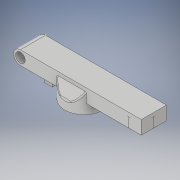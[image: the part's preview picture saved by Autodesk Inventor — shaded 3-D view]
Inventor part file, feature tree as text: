
AUTODESK INVENTOR PART (.ipt)
format: ipt  version: 2019 (Build 230136000, 136)  size: 247,808 bytes
history: native  units: in
note: dims shown in document units (in); Inventor stores cm internally (conversion verified against a paired STEP export)
features: sketch x9, extrude x5, chamfer x2, fillet x2
ambient origin geometry x8: Origin, YZ Plane, XZ Plane, XY Plane, X Axis, Y Axis, Z Axis, Center Point
bodies: Solid1 (feature_tree)
feature tree (18):
  extrude  "Extrusion1"  Depth=2.4606in
  extrude  "Extrusion2"  Depth=0.5118in TaperAngle=0.0deg
  extrude  "Extrusion3"  Depth=0.1969in TaperAngle=0.0deg
  sketch  "Sketch4"  dims[d9=2.2047in]
  chamfer  "Chamfer1"  Distance=0.1969in
  chamfer  "Chamfer2"  Distance=0.1181in Angle=120.0deg
  extrude  "Extrusion4"  Depth=0.2362in TaperAngle=0.0deg
  fillet  "Fillet2"  Radius=0.0394in
  fillet  "Fillet3"  Radius=0.0394in
  sketch  "Sketch6"  dims[d15=0.2559in]
  sketch  "Sketch7"  dims[d16=0.2559in d17=0.1181in d18=0.0787in d19=120.0deg]
  sketch  "Sketch8"  dims[d20=0.1181in d21=0.0787in d22=120.0deg d25=0.2362in d26=0.0in d28=0.0394in d29=0.0394in]
  sketch  "Sketch9"  dims[d30=1.1811in d32=0.1575in d33=0.1575in d34=0.315in d35=0.1772in d36=0.0394in d37=0.0787in d39=0.1496in d41=0.1102in d42=0.1575in d43=0.0in]
  extrude  "Extrusion5"  Depth=0.1575in
  sketch  "Sketch1"  dims[d0=0.1969in d2=2.4606in]
  sketch  "Sketch2"  dims[d3=0.1378in d4=0.5118in d5=0.0in]
  sketch  "Sketch3"  dims[d6=0.5118in d7=0.1969in d8=0.0in]
  sketch  "Sketch5"  dims[d11=0.7874in d13=0.1969in d14=0.0in]
